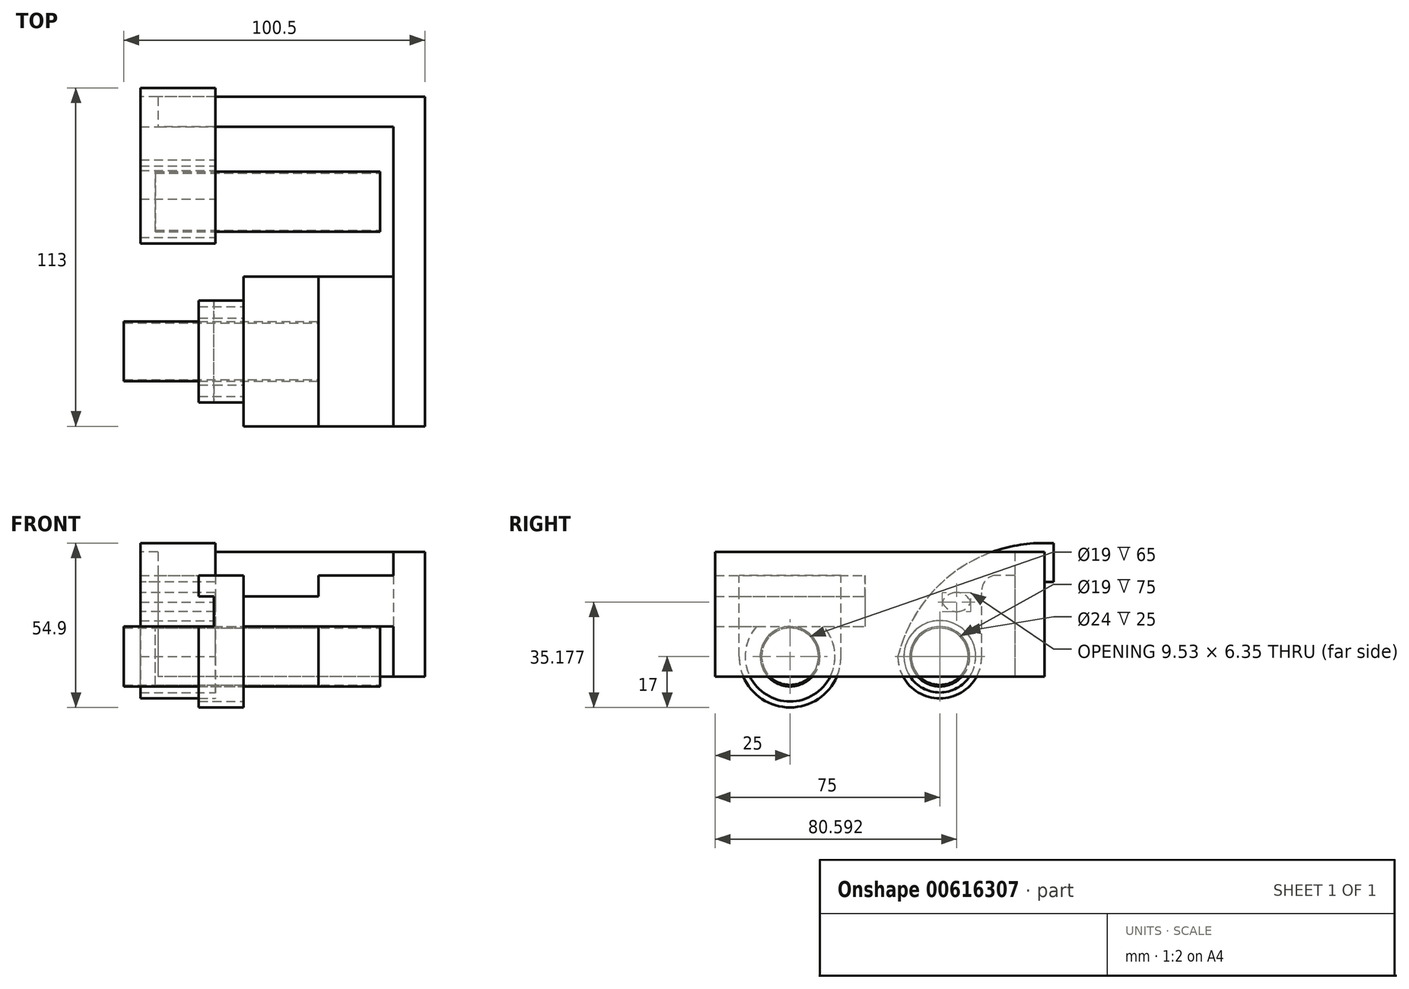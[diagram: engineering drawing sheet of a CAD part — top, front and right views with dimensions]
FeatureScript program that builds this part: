
annotation { "Feature Type Name" : "Feature", "Feature Type Description" : "" }
export const myFeature = defineFeature(function(context is Context, id is Id, definition is map)
    precondition{}
    {
        {
            var Q0;
            Q0=qCreatedBy(makeId("Front.planeOp"),FACE);
            var sketch = newSketch(context, id + "F0", { "sketchPlane" : qUnion([Q0])});
            skLineSegment(sketch, "E0.bottom", {"start": v(-30.5, 5.1) * mm, "end": v(30, 5.1) * mm});
            skLineSegment(sketch, "E0.top", {"start": v(-30.5, -5) * mm, "end": v(30, -5) * mm});
            skLineSegment(sketch, "E0.left", {"start": v(-30.5, 5.1) * mm, "end": v(-30.5, -5) * mm});
            skPoint(sketch, "E0.middle", {"position": v(0, 0) * mm});
            skLineSegment(sketch, "E1.bottom", {"start": v(-5.5, 5.1) * mm, "end": v(30, 5.1) * mm});
            skLineSegment(sketch, "E1.top", {"start": v(-5.5, 12.1) * mm, "end": v(30, 12.1) * mm});
            skLineSegment(sketch, "E1.left", {"start": v(-5.5, 5.1) * mm, "end": v(-5.5, 12.1) * mm});
            skLineSegment(sketch, "E2", {"start": v(19.5, 5.1) * mm, "end": v(19.5, 12.1) * mm});
            skLineSegment(sketch, "E3", {"start": v(30, -5) * mm, "end": v(30, 19.9) * mm});
            skLineSegment(sketch, "E4", {"start": v(30, 19.9) * mm, "end": v(19.5, 19.9) * mm});
            skLineSegment(sketch, "E5", {"start": v(19.5, 19.9) * mm, "end": v(19.5, -5) * mm});
            skLineSegment(sketch, "E6.bottom", {"start": v(19.5, -5) * mm, "end": v(30, -5) * mm});
            skLineSegment(sketch, "E6.top", {"start": v(19.5, -21.67) * mm, "end": v(30, -21.67) * mm});
            skLineSegment(sketch, "E6.left", {"start": v(19.5, -5) * mm, "end": v(19.5, -21.67) * mm});
            skLineSegment(sketch, "E6.right", {"start": v(30, -5) * mm, "end": v(30, -21.67) * mm});
            skSolve(sketch);
        }
        {
            var Q0;
            {var subQ0=sQuery(id+"F0.wireOp",EDGE,"E0.left");var subQ5=sQuery(id+"F0.wireOp",EDGE,"E2");var subQ6=sQuery(id+"F0.wireOp",EDGE,"E0.bottom");var subQ9=sQuery(id+"F0.wireOp",EDGE,"E1.left");var subQ12=sQuery(id+"F0.wireOp",EDGE,"E3");var subQ13=makeQuery(id+"F0.imprint","INTERSECT",VERTEX,{"derivedFrom":[subQ6,subQ12]});var subQ14=makeQuery(id+"F0.imprint","IMPRINT",EDGE,{"disambiguationData":[TD([[subQ13,1.0]])],"derivedFrom":subQ6});var subQ19=makeQuery(id+"F0.imprint","IMPRINT",EDGE,{"derivedFrom":subQ5});var subQ20=sQuery(id+"F0.wireOp",EDGE,"E4");Q0=qUnion([makeQuery(id+"F0.imprint","IMPRINT",FACE,{"disambiguationData":[TD([[makeQuery(id+"F0.imprint","IMPRINT",EDGE,{"derivedFrom":subQ9}),-1.0]])]}),makeQuery(id+"F0.imprint","IMPRINT",FACE,{"disambiguationData":[TD([[makeQuery(id+"F0.imprint","IMPRINT",EDGE,{"derivedFrom":sQuery(id+"F0.wireOp",EDGE,"E6.top")}),1.0]])]}),makeQuery(id+"F0.imprint","IMPRINT",FACE,{"disambiguationData":[TD([[subQ14,-1.0]])]}),makeQuery(id+"F0.imprint","IMPRINT",FACE,{"disambiguationData":[TD([[makeQuery(id+"F0.imprint","IMPRINT",EDGE,{"derivedFrom":subQ20}),1.0]])]}),makeQuery(id+"F0.imprint","IMPRINT",FACE,{"disambiguationData":[TD([[subQ19,-1.0]])]}),makeQuery(id+"F0.imprint","IMPRINT",FACE,{"disambiguationData":[TD([[makeQuery(id+"F0.imprint","IMPRINT",EDGE,{"derivedFrom":subQ0}),1.0]])]})]);}
            extrude(context, id + "F1", {"entities" : qUnion([Q0]), "depth" : 25 * mm, "offsetDistance" : 25 * mm, "hasSecondDirection" : true, "secondDirectionOppositeDirection" : true, "secondDirectionDepth" : 25 * mm});
        }
        {
            var Q0;
            Q0=makeQuery(id+"F1.opExtrude","CAP_FACE",FACE,{"disambiguationData":[OSD([sQuery(id+"F0.wireOp",EDGE,"E0.bottom"),sQuery(id+"F0.wireOp",EDGE,"E0.top"),sQuery(id+"F0.wireOp",EDGE,"E0.left"),sQuery(id+"F0.wireOp",EDGE,"E1.top"),sQuery(id+"F0.wireOp",EDGE,"E1.left"),sQuery(id+"F0.wireOp",EDGE,"E3"),sQuery(id+"F0.wireOp",EDGE,"E4"),sQuery(id+"F0.wireOp",EDGE,"E5"),sQuery(id+"F0.wireOp",EDGE,"E6.top"),sQuery(id+"F0.wireOp",EDGE,"E6.left"),sQuery(id+"F0.wireOp",EDGE,"E6.right")])],"isStart":true});
            var sketch = newSketch(context, id + "F2", { "sketchPlane" : qUnion([Q0])});
            skLineSegment(sketch, "E7.0.0", {"start": v(-19.5, 12.1) * mm, "end": v(-19.5, 19.9) * mm, "construction": true});
            skLineSegment(sketch, "E7.0.1", {"start": v(-19.5, 19.9) * mm, "end": v(-30, 19.9) * mm, "construction": true});
            skLineSegment(sketch, "E7.0.2", {"start": v(-30, 19.9) * mm, "end": v(-30, -21.67) * mm, "construction": true});
            skLineSegment(sketch, "E7.0.3", {"start": v(-30, -21.67) * mm, "end": v(-19.5, -21.67) * mm, "construction": true});
            skLineSegment(sketch, "E7.0.4", {"start": v(-19.5, -21.67) * mm, "end": v(-19.5, -5) * mm, "construction": true});
            skLineSegment(sketch, "E7.0.5", {"start": v(-19.5, -5) * mm, "end": v(30.5, -5) * mm, "construction": true});
            skLineSegment(sketch, "E7.0.6", {"start": v(30.5, -5) * mm, "end": v(30.5, 5.1) * mm, "construction": true});
            skLineSegment(sketch, "E7.0.7", {"start": v(30.5, 5.1) * mm, "end": v(5.5, 5.1) * mm, "construction": true});
            skLineSegment(sketch, "E7.0.8", {"start": v(5.5, 5.1) * mm, "end": v(5.5, 12.1) * mm, "construction": true});
            skLineSegment(sketch, "E7.0.9", {"start": v(5.5, 12.1) * mm, "end": v(-19.5, 12.1) * mm, "construction": true});
            skLineSegment(sketch, "E8.bottom", {"start": v(-30, 19.9) * mm, "end": v(-19.5, 19.9) * mm});
            skLineSegment(sketch, "E8.top", {"start": v(-30, -21.67) * mm, "end": v(-19.5, -21.67) * mm});
            skLineSegment(sketch, "E8.left", {"start": v(-30, 19.9) * mm, "end": v(-30, -21.67) * mm});
            skLineSegment(sketch, "E8.right", {"start": v(-19.5, 19.9) * mm, "end": v(-19.5, -21.67) * mm});
            skSolve(sketch);
        }
        {
            var Q0;
            Q0=qSketchRegion(id+"F2",true);
            extrude(context, id + "F3", {"entities" : qUnion([Q0]), "operationType" : NewBodyOperationType.ADD, "depth" : 50 * mm, "offsetDistance" : 25 * mm});
        }
        {
            var Q0;
            Q0=makeQuery(id+"F3.opExtrude","CAP_FACE",FACE,{"disambiguationData":[OSD([sQuery(id+"F2.wireOp",EDGE,"E8.bottom"),sQuery(id+"F2.wireOp",EDGE,"E8.top"),sQuery(id+"F2.wireOp",EDGE,"E8.left"),sQuery(id+"F2.wireOp",EDGE,"E8.right")])],"isStart":false});
            var sketch = newSketch(context, id + "F4", { "sketchPlane" : qUnion([Q0])});
            skLineSegment(sketch, "E9.0.0", {"start": v(-19.5, -21.67) * mm, "end": v(-19.5, 19.9) * mm, "construction": true});
            skLineSegment(sketch, "E9.0.1", {"start": v(-19.5, 19.9) * mm, "end": v(-30, 19.9) * mm, "construction": true});
            skLineSegment(sketch, "E9.0.2", {"start": v(-30, 19.9) * mm, "end": v(-30, -21.67) * mm, "construction": true});
            skLineSegment(sketch, "E9.0.3", {"start": v(-30, -21.67) * mm, "end": v(-19.5, -21.67) * mm, "construction": true});
            skLineSegment(sketch, "E10.bottom", {"start": v(-30, 19.9) * mm, "end": v(59.17, 19.9) * mm});
            skLineSegment(sketch, "E10.top", {"start": v(-30, -21.67) * mm, "end": v(59.17, -21.67) * mm});
            skLineSegment(sketch, "E10.left", {"start": v(-30, 19.9) * mm, "end": v(-30, -21.67) * mm});
            skLineSegment(sketch, "E10.right", {"start": v(59.17, 19.9) * mm, "end": v(59.17, -21.67) * mm});
            skSolve(sketch);
        }
        {
            var Q0;
            Q0=qSketchRegion(id+"F4",true);
            extrude(context, id + "F5", {"entities" : qUnion([Q0]), "operationType" : NewBodyOperationType.ADD, "depth" : 10 * mm, "offsetDistance" : 25 * mm});
        }
        {
            var Q0;
            Q0=makeQuery(id+"F1.opExtrude","SWEPT_FACE",FACE,{"disambiguationData":[OSD([sQuery(id+"F0.wireOp",EDGE,"E0.left")])]});
            var sketch = newSketch(context, id + "F6", { "sketchPlane" : qUnion([Q0])});
            skPoint(sketch, "E11", {"position": v(0, -15) * mm});
            skLineSegment(sketch, "E12.0", {"start": v(25, -5) * mm, "end": v(-25, -5) * mm, "construction": true});
            skCircle(sketch, "E13", {"center": v(0, -15) * mm, "radius": 10 * mm});
            skCircle(sketch, "E14", {"center": v(0, -15) * mm, "radius": 9.5 * mm});
            skSolve(sketch);
        }
        {
            var Q0;
            Q0=qSketchRegion(id+"F6",true);
            extrude(context, id + "F7", {"entities" : qUnion([Q0]), "depth" : 40 * mm, "offsetDistance" : 25 * mm, "hasSecondDirection" : true, "secondDirectionOppositeDirection" : true, "secondDirectionDepth" : 25 * mm});
        }
        {
            var Q0;
            Q0=makeQuery(id+"F1.opExtrude","SWEPT_FACE",FACE,{"disambiguationData":[OSD([sQuery(id+"F0.wireOp",EDGE,"E0.left")])]});
            var sketch = newSketch(context, id + "F8", { "sketchPlane" : qUnion([Q0])});
            skCircle(sketch, "E15.0", {"center": v(0, -15) * mm, "radius": 10 * mm, "construction": true});
            skLineSegment(sketch, "E16.0", {"start": v(25, -5) * mm, "end": v(-25, -5) * mm, "construction": true});
            skLineSegment(sketch, "E17.0", {"start": v(25, 5.1) * mm, "end": v(-25, 5.1) * mm, "construction": true});
            skCircle(sketch, "E18", {"center": v(0, -15) * mm, "radius": 15 * mm});
            skCircle(sketch, "E19", {"center": v(0, -15) * mm, "radius": 17 * mm});
            skLineSegment(sketch, "E20", {"start": v(0, -15) * mm, "end": v(20.33, -15) * mm, "construction": true});
            skLineSegment(sketch, "E21", {"start": v(17, -15) * mm, "end": v(17, -5) * mm});
            skLineSegment(sketch, "E22", {"start": v(-17, -15) * mm, "end": v(-17, -5) * mm});
            skLineSegment(sketch, "E23", {"start": v(-17, -5) * mm, "end": v(17, -5) * mm});
            skLineSegment(sketch, "E24", {"start": v(-17, -5) * mm, "end": v(-17, 5.1) * mm});
            skLineSegment(sketch, "E25", {"start": v(-17, 5.1) * mm, "end": v(17, 5.1) * mm});
            skLineSegment(sketch, "E26", {"start": v(17, 5.1) * mm, "end": v(17, -5) * mm});
            skLineSegment(sketch, "E27.0", {"start": v(25, 12.1) * mm, "end": v(-25, 12.1) * mm, "construction": true});
            skLineSegment(sketch, "E28", {"start": v(-17, 5.1) * mm, "end": v(-17, 12.1) * mm});
            skLineSegment(sketch, "E29", {"start": v(-17, 12.1) * mm, "end": v(17, 12.1) * mm});
            skLineSegment(sketch, "E30", {"start": v(17, 12.1) * mm, "end": v(17, 5.1) * mm});
            skSolve(sketch);
        }
        {
            var Q0;
            {var subQ3=sQuery(id+"F8.wireOp",EDGE,"E23");var subQ6=sQuery(id+"F8.wireOp",EDGE,"E18");var subQ7=makeQuery(id+"F8.imprint","INTERSECT",VERTEX,{"disambiguationData":[OD(0.0)],"derivedFrom":[subQ6,subQ3]});Q0=makeQuery(id+"F8.imprint","IMPRINT",FACE,{"disambiguationData":[TD([[makeQuery(id+"F8.imprint","IMPRINT",EDGE,{"disambiguationData":[TD([[subQ7,1.0]])],"derivedFrom":subQ6}),-1.0]])]});}
            var Q1;
            {var subQ0=sQuery(id+"F8.wireOp",EDGE,"E22");Q1=makeQuery(id+"F8.imprint","IMPRINT",FACE,{"disambiguationData":[TD([[makeQuery(id+"F8.imprint","IMPRINT",EDGE,{"derivedFrom":subQ0}),-1.0]])]});}
            var Q2;
            {var subQ0=sQuery(id+"F8.wireOp",EDGE,"E21");Q2=makeQuery(id+"F8.imprint","IMPRINT",FACE,{"disambiguationData":[TD([[makeQuery(id+"F8.imprint","IMPRINT",EDGE,{"derivedFrom":subQ0}),1.0]])]});}
            var Q3;
            {var subQ0=sQuery(id+"F8.wireOp",EDGE,"E24");Q3=makeQuery(id+"F8.imprint","IMPRINT",FACE,{"disambiguationData":[TD([[makeQuery(id+"F8.imprint","IMPRINT",EDGE,{"derivedFrom":subQ0}),-1.0]])]});}
            var Q4;
            {var subQ0=sQuery(id+"F8.wireOp",EDGE,"E23");var subQ1=sQuery(id+"F8.wireOp",EDGE,"E18");var subQ2=makeQuery(id+"F8.imprint","INTERSECT",VERTEX,{"disambiguationData":[OD(0.0)],"derivedFrom":[subQ1,subQ0]});Q4=makeQuery(id+"F8.imprint","IMPRINT",FACE,{"disambiguationData":[TD([[makeQuery(id+"F8.imprint","IMPRINT",EDGE,{"disambiguationData":[TD([[subQ2,-1.0]])],"derivedFrom":subQ1}),-1.0]])]});}
            var Q5;
            {var subQ0=sQuery(id+"F8.wireOp",EDGE,"E23");var subQ1=sQuery(id+"F8.wireOp",EDGE,"E18");var subQ2=makeQuery(id+"F8.imprint","INTERSECT",VERTEX,{"disambiguationData":[OD(0.0)],"derivedFrom":[subQ1,subQ0]});Q5=makeQuery(id+"F8.imprint","IMPRINT",FACE,{"disambiguationData":[TD([[makeQuery(id+"F8.imprint","IMPRINT",EDGE,{"disambiguationData":[TD([[subQ2,-1.0]])],"derivedFrom":subQ1}),1.0]])]});}
            var Q6;
            Q6=makeQuery(id+"F8.imprint","IMPRINT",FACE,{"disambiguationData":[TD([[makeQuery(id+"F8.imprint","IMPRINT",EDGE,{"derivedFrom":sQuery(id+"F8.wireOp",EDGE,"E25")}),-1.0]])]});
            extrude(context, id + "F9", {"entities" : qUnion([Q0, Q1, Q2, Q3, Q4, Q5, Q6]), "depth" : 10 * mm, "offsetDistance" : 25 * mm});
        }
        {
            var Q0;
            Q0=makeQuery(id+"F9.opExtrude","CAP_FACE",FACE,{"disambiguationData":[OSD([sQuery(id+"F8.wireOp",EDGE,"E18"),sQuery(id+"F8.wireOp",EDGE,"E19"),sQuery(id+"F8.wireOp",EDGE,"E21"),sQuery(id+"F8.wireOp",EDGE,"E22"),sQuery(id+"F8.wireOp",EDGE,"E23"),sQuery(id+"F8.wireOp",EDGE,"E24"),sQuery(id+"F8.wireOp",EDGE,"E26"),sQuery(id+"F8.wireOp",EDGE,"E28"),sQuery(id+"F8.wireOp",EDGE,"E29"),sQuery(id+"F8.wireOp",EDGE,"E30")])],"isStart":true});
            var sketch = newSketch(context, id + "F10", { "sketchPlane" : qUnion([Q0])});
            skLineSegment(sketch, "E31.0", {"start": v(-25, 12.1) * mm, "end": v(25, 12.1) * mm, "construction": true});
            skLineSegment(sketch, "E32.0", {"start": v(-25, 5.1) * mm, "end": v(25, 5.1) * mm, "construction": true});
            skLineSegment(sketch, "E33.0", {"start": v(17, -15) * mm, "end": v(17, 12.1) * mm, "construction": true});
            skLineSegment(sketch, "E34.0", {"start": v(-17, -15) * mm, "end": v(-17, 12.1) * mm, "construction": true});
            skLineSegment(sketch, "E35.bottom", {"start": v(17, 12.1) * mm, "end": v(-17, 12.1) * mm});
            skLineSegment(sketch, "E35.top", {"start": v(17, 5.1) * mm, "end": v(-17, 5.1) * mm});
            skLineSegment(sketch, "E35.left", {"start": v(17, 12.1) * mm, "end": v(17, 5.1) * mm});
            skLineSegment(sketch, "E35.right", {"start": v(-17, 12.1) * mm, "end": v(-17, 5.1) * mm});
            skArc(sketch, "E36.0", {"start": v(11.18, -5) * mm, "mid": v(0, -30) * mm, "end": v(-11.18, -5) * mm});
            skLineSegment(sketch, "E37.0", {"start": v(-25, -5) * mm, "end": v(25, -5) * mm, "construction": true});
            skPoint(sketch, "E38.0", {"position": v(17, -15) * mm});
            skPoint(sketch, "E39.0", {"position": v(-17, -15) * mm});
            skArc(sketch, "E40.0", {"start": v(17, -15) * mm, "mid": v(0, -32) * mm, "end": v(-17, -15) * mm});
            skArc(sketch, "E41.0.0", {"start": v(-17, -15) * mm, "mid": v(0, -32) * mm, "end": v(17, -15) * mm, "construction": true});
            skLineSegment(sketch, "E41.0.2", {"start": v(17, 12.1) * mm, "end": v(-17, 12.1) * mm, "construction": true});
            skLineSegment(sketch, "E41.0.3", {"start": v(-17, 12.1) * mm, "end": v(-17, -15) * mm, "construction": true});
            skLineSegment(sketch, "E42", {"start": v(-17, -15) * mm, "end": v(-17, -5) * mm});
            skLineSegment(sketch, "E43", {"start": v(-17, -5) * mm, "end": v(17, -5) * mm});
            skLineSegment(sketch, "E44", {"start": v(17, -5) * mm, "end": v(17, -15) * mm});
            skSolve(sketch);
        }
        {
            var Q0;
            Q0=makeQuery(id+"F10.imprint","IMPRINT",FACE,{"disambiguationData":[TD([[makeQuery(id+"F10.imprint","IMPRINT",EDGE,{"derivedFrom":sQuery(id+"F10.wireOp",EDGE,"E35.bottom")}),1.0]])]});
            var Q1;
            {var subQ1=sQuery(id+"F10.wireOp",EDGE,"E36.0");Q1=makeQuery(id+"F10.imprint","IMPRINT",FACE,{"disambiguationData":[TD([[makeQuery(id+"F10.imprint","IMPRINT",EDGE,{"derivedFrom":subQ1}),1.0]])]});}
            extrude(context, id + "F11", {"entities" : qUnion([Q0, Q1]), "operationType" : NewBodyOperationType.ADD, "oppositeDirection" : true, "depth" : 15 * mm, "offsetDistance" : 25 * mm});
        }
        {
            var Q0;
            Q0=qCreatedBy(makeId("Right.planeOp"),FACE);
            var sketch = newSketch(context, id + "F12", { "sketchPlane" : qUnion([Q0])});
            skLineSegment(sketch, "E45", {"start": v(0, 0) * mm, "end": v(71.15, 0) * mm, "construction": true});
            skCircle(sketch, "E46.0", {"center": v(0, -15) * mm, "radius": 9.5 * mm, "construction": true});
            skCircle(sketch, "E47.0", {"center": v(0, -15) * mm, "radius": 10 * mm, "construction": true});
            skLineSegment(sketch, "E48", {"start": v(0, -15) * mm, "end": v(68.73, -15) * mm, "construction": true});
            skLineSegment(sketch, "E49.0", {"start": v(75, 19.9) * mm, "end": v(75, -21.67) * mm, "construction": true});
            skLineSegment(sketch, "E50.0", {"start": v(25, 5.1) * mm, "end": v(25, -5) * mm, "construction": true});
            skCircle(sketch, "E51", {"center": v(50, -15) * mm, "radius": 9.5 * mm});
            skCircle(sketch, "E52", {"center": v(50, -15) * mm, "radius": 10 * mm});
            skSolve(sketch);
        }
        {
            var Q0;
            Q0=qSketchRegion(id+"F12",true);
            extrude(context, id + "F13", {"entities" : qUnion([Q0]), "oppositeDirection" : true, "depth" : 60 * mm, "offsetDistance" : 25 * mm, "hasSecondDirection" : true, "secondDirectionOppositeDirection" : false, "secondDirectionDepth" : 15 * mm});
        }
        {
            var Q0;
            Q0=qCreatedBy(makeId("Right.planeOp"),FACE);
            cPlane(context, id + "F14", {"entities" : qUnion([Q0]), "cplaneType" : CPlaneType.OFFSET, "offset" : 40 * mm, "oppositeDirection" : true, "width" : 150 * mm, "height" : 150 * mm});
        }
        {
            var Q0;
            Q0=qCreatedBy(id+"F14.planeOp",FACE);
            var sketch = newSketch(context, id + "F15", { "sketchPlane" : qUnion([Q0])});
            skCircle(sketch, "E53.0", {"center": v(50, -15) * mm, "radius": 9.5 * mm});
            skCircle(sketch, "E54.0", {"center": v(50, -15) * mm, "radius": 10 * mm});
            skCircle(sketch, "E55", {"center": v(50, -15) * mm, "radius": 12 * mm});
            skCircle(sketch, "E56", {"center": v(50, -15) * mm, "radius": 14 * mm});
            skLineSegment(sketch, "E57.0", {"start": v(-25, 12.1) * mm, "end": v(10, 12.1) * mm, "construction": true});
            skLineSegment(sketch, "E58.0", {"start": v(75, 12.1) * mm, "end": v(75, -21.67) * mm, "construction": true});
            skLineSegment(sketch, "E59", {"start": v(36, -15) * mm, "end": v(36, 12.1) * mm});
            skLineSegment(sketch, "E60", {"start": v(64, -15) * mm, "end": v(64, 12.1) * mm});
            skLineSegment(sketch, "E61", {"start": v(64, 12.1) * mm, "end": v(36, 12.1) * mm});
            skLineSegment(sketch, "E62.top", {"start": v(75, 12.1) * mm, "end": v(36, 12.1) * mm});
            skLineSegment(sketch, "E63.0.1", {"start": v(10, 5.1) * mm, "end": v(-25, 5.1) * mm, "construction": true});
            skLineSegment(sketch, "E63.0.2", {"start": v(-25, 5.1) * mm, "end": v(-25, 12.1) * mm, "construction": true});
            skPoint(sketch, "E62.left.start.orphan", {"position": v(75, 19.9) * mm});
            skLineSegment(sketch, "E64.right", {"start": v(36, 12.1) * mm, "end": v(36, 5.1) * mm});
            skLineSegment(sketch, "E65.left", {"start": v(75, 19.9) * mm, "end": v(75, 12.1) * mm});
            skLineSegment(sketch, "E66", {"start": v(75, 19.9) * mm, "end": v(36, 12.1) * mm});
            skLineSegment(sketch, "E67.bottom", {"start": v(75, 19.9) * mm, "end": v(36, 19.9) * mm});
            skLineSegment(sketch, "E67.right", {"start": v(36, 19.9) * mm, "end": v(36, 12.1) * mm});
            skPoint(sketch, "E63.0.0.end.orphan", {"position": v(25, 5.1) * mm});
            skPoint(sketch, "E63.0.0.start.orphan", {"position": v(25, 12.1) * mm});
            skSolve(sketch);
        }
        {
            var Q0;
            Q0=qSketchRegion(id+"F15",true);
            var Q1;
            Q1=makeQuery(id+"F3.boolean.opBoolean","MERGE",FACE,{"derivedFrom":[makeQuery(id+"F1.opExtrude","SWEPT_FACE",FACE,{"disambiguationData":[OSD([sQuery(id+"F0.wireOp",EDGE,"E5")])]}),makeQuery(id+"F1.opExtrude","SWEPT_FACE",FACE,{"disambiguationData":[OSD([sQuery(id+"F0.wireOp",EDGE,"E6.left")])]}),makeQuery(id+"F3.opExtrude","SWEPT_FACE",FACE,{"disambiguationData":[OSD([sQuery(id+"F2.wireOp",EDGE,"E8.right")])]})]});
            extrude(context, id + "F16", {"entities" : qUnion([Q0]), "oppositeDirection" : true, "depth" : 25 * mm, "endBoundEntityFace" : qUnion([Q1]), "offsetDistance" : 25 * mm});
        }
        {
            var Q0;
            Q0=makeQuery(id+"F16.opExtrude","SWEPT_FACE",FACE,{"disambiguationData":[OSD([sQuery(id+"F15.wireOp",EDGE,"E67.bottom")])]});
            var sketch = newSketch(context, id + "F17", { "sketchPlane" : qUnion([Q0])});
            skLineSegment(sketch, "E68.0.0", {"start": v(30, -25) * mm, "end": v(30, 85) * mm, "construction": true});
            skLineSegment(sketch, "E68.0.1", {"start": v(30, 85) * mm, "end": v(-59.17, 85) * mm, "construction": true});
            skLineSegment(sketch, "E68.0.2", {"start": v(-59.17, 85) * mm, "end": v(-59.17, 75) * mm, "construction": true});
            skLineSegment(sketch, "E68.0.3", {"start": v(-59.17, 75) * mm, "end": v(19.5, 75) * mm, "construction": true});
            skLineSegment(sketch, "E68.0.4", {"start": v(19.5, 75) * mm, "end": v(19.5, -25) * mm, "construction": true});
            skLineSegment(sketch, "E68.0.5", {"start": v(19.5, -25) * mm, "end": v(30, -25) * mm, "construction": true});
            skLineSegment(sketch, "E69", {"start": v(15, 40) * mm, "end": v(-60, 40) * mm, "construction": true});
            skLineSegment(sketch, "E70", {"start": v(-60, 60) * mm, "end": v(15, 60) * mm, "construction": true});
            skLineSegment(sketch, "E71.bottom", {"start": v(-40, 36) * mm, "end": v(-65, 36) * mm});
            skLineSegment(sketch, "E71.top", {"start": v(-40, 85) * mm, "end": v(-65, 85) * mm});
            skLineSegment(sketch, "E71.left", {"start": v(-40, 36) * mm, "end": v(-40, 85) * mm});
            skLineSegment(sketch, "E71.right", {"start": v(-65, 36) * mm, "end": v(-65, 85) * mm});
            skSolve(sketch);
        }
        {
            var Q0;
            Q0=qSketchRegion(id+"F17",true);
            extrude(context, id + "F18", {"entities" : qUnion([Q0]), "operationType" : NewBodyOperationType.ADD, "depth" : 3 * mm, "offsetDistance" : 25 * mm});
        }
        {
            var Q0;
            Q0=makeQuery(id+"F18.opExtrude","SWEPT_FACE",FACE,{"disambiguationData":[OSD([sQuery(id+"F17.wireOp",EDGE,"E71.top")])]});
            var sketch = newSketch(context, id + "F19", { "sketchPlane" : qUnion([Q0])});
            skLineSegment(sketch, "E72.0.0", {"start": v(40, 19.9) * mm, "end": v(65, 19.9) * mm, "construction": true});
            skLineSegment(sketch, "E72.0.1", {"start": v(65, 19.9) * mm, "end": v(65, 22.9) * mm, "construction": true});
            skLineSegment(sketch, "E72.0.2", {"start": v(65, 22.9) * mm, "end": v(40, 22.9) * mm, "construction": true});
            skLineSegment(sketch, "E72.0.3", {"start": v(40, 22.9) * mm, "end": v(40, 19.9) * mm, "construction": true});
            skLineSegment(sketch, "E73.bottom", {"start": v(40, 22.9) * mm, "end": v(65, 22.9) * mm});
            skLineSegment(sketch, "E73.top", {"start": v(40, 9.9) * mm, "end": v(65, 9.9) * mm});
            skLineSegment(sketch, "E73.left", {"start": v(40, 22.9) * mm, "end": v(40, 9.9) * mm});
            skLineSegment(sketch, "E73.right", {"start": v(65, 22.9) * mm, "end": v(65, 9.9) * mm});
            skSolve(sketch);
        }
        {
            var Q0;
            Q0=qSketchRegion(id+"F19",true);
            extrude(context, id + "F20", {"entities" : qUnion([Q0]), "operationType" : NewBodyOperationType.ADD, "depth" : 3 * mm, "offsetDistance" : 25 * mm});
        }
        {
            var Q0;
            Q0=makeQuery(id+"F18.opExtrude","CAP_EDGE",EDGE,{"disambiguationData":[OSD([sQuery(id+"F17.wireOp",EDGE,"E71.bottom")])],"isStart":false});
            fillet(context, id + "F21", {"entities" : qUnion([Q0]), "radius" : 50 * mm, "tangentPropagation" : true, "allowEdgeOverflow" : false});
        }
        {
            var Q0;
            Q0=makeQuery(id+"F20.boolean.opBoolean","MERGE",FACE,{"derivedFrom":[makeQuery(id+"F18.boolean.opBoolean","MERGE",FACE,{"derivedFrom":[makeQuery(id+"F16.opExtrude","CAP_FACE",FACE,{"disambiguationData":[OSD([sQuery(id+"F15.wireOp",EDGE,"E55"),sQuery(id+"F15.wireOp",EDGE,"E56"),sQuery(id+"F15.wireOp",EDGE,"E59"),sQuery(id+"F15.wireOp",EDGE,"E60"),sQuery(id+"F15.wireOp",EDGE,"E64.bottom"),sQuery(id+"F15.wireOp",EDGE,"E64.top"),sQuery(id+"F15.wireOp",EDGE,"E64.left"),sQuery(id+"F15.wireOp",EDGE,"E67.bottom"),sQuery(id+"F15.wireOp",EDGE,"E62.top"),sQuery(id+"F15.wireOp",EDGE,"E65.left"),sQuery(id+"F15.wireOp",EDGE,"E67.right")])],"isStart":false}),makeQuery(id+"F18.opExtrude","SWEPT_FACE",FACE,{"disambiguationData":[OSD([sQuery(id+"F17.wireOp",EDGE,"E71.right")])]})]}),makeQuery(id+"F20.opExtrude","SWEPT_FACE",FACE,{"disambiguationData":[OSD([sQuery(id+"F19.wireOp",EDGE,"E73.right")])]})]});
            var sketch = newSketch(context, id + "F22", { "sketchPlane" : qUnion([Q0])});
            skLineSegment(sketch, "E74.0", {"start": v(-13.3, 8.4) * mm, "end": v(-13.3, 8.8) * mm});
            skLineSegment(sketch, "E74.3", {"start": v(-50.48, 0) * mm, "end": v(-50.48, 8.4) * mm});
            skLineSegment(sketch, "E74.5", {"start": v(-60.7, 6.35) * mm, "end": v(-60.7, 0) * mm});
            skLineSegment(sketch, "E75", {"start": v(-50.48, 6.35) * mm, "end": v(-50.48, 8.4) * mm});
            skLineSegment(sketch, "E76", {"start": v(-50.48, 6.35) * mm, "end": v(-60.7, 6.35) * mm});
            skLineSegment(sketch, "E77", {"start": v(-60.7, 0) * mm, "end": v(-50.48, 0) * mm});
            skSolve(sketch);
        }
        {
            var Q0;
            Q0=makeQuery(id+"F22.imprint","IMPRINT",FACE,{"disambiguationData":[TD([[makeQuery(id+"F22.imprint","IMPRINT",EDGE,{"derivedFrom":sQuery(id+"F22.wireOp",EDGE,"E74.5")}),1.0]])]});
            extrude(context, id + "F23", {"entities" : qUnion([Q0]), "operationType" : NewBodyOperationType.REMOVE, "oppositeDirection" : true, "depth" : 25 * mm, "offsetDistance" : 25 * mm});
        }
        {
            var Q0;
            {var subQ0=sQuery(id+"F22.wireOp",EDGE,"E76");Q0=qUnion([makeQuery(id+"F23.boolean.opBoolean","COPY",EDGE,{"derivedFrom":makeQuery(id+"F23.opExtrude","SWEPT_EDGE",EDGE,{"disambiguationData":[OSD([sQuery(id+"F22.wireOp",EDGE,"E74.3"),subQ0])]})}),makeQuery(id+"F23.boolean.opBoolean","COPY",EDGE,{"derivedFrom":makeQuery(id+"F23.opExtrude","SWEPT_EDGE",EDGE,{"disambiguationData":[OSD([sQuery(id+"F22.wireOp",EDGE,"E74.5"),subQ0])]})})]);}
            var Q1;
            Q1=makeQuery(id+"F16.opExtrude","SWEPT_EDGE",EDGE,{"disambiguationData":[OSD([sQuery(id+"F15.wireOp",EDGE,"E59"),sQuery(id+"F15.wireOp",EDGE,"E64.top"),sQuery(id+"F15.wireOp",EDGE,"E64.right")])]});
            var Q2;
            Q2=makeQuery(id+"F16.opExtrude","SWEPT_EDGE",EDGE,{"disambiguationData":[OSD([sQuery(id+"F15.wireOp",EDGE,"E60"),sQuery(id+"F15.wireOp",EDGE,"E62.top")])]});
            var Q3;
            Q3=makeQuery(id+"F23.boolean.opBoolean","COPY",EDGE,{"derivedFrom":makeQuery(id+"F23.opExtrude","SWEPT_EDGE",EDGE,{"disambiguationData":[OSD([sQuery(id+"F22.wireOp",EDGE,"E74.5"),sQuery(id+"F22.wireOp",EDGE,"E76")])]})});
            var Q4;
            Q4=makeQuery(id+"F23.boolean.opBoolean","COPY",EDGE,{"derivedFrom":makeQuery(id+"F23.opExtrude","SWEPT_EDGE",EDGE,{"disambiguationData":[OSD([sQuery(id+"F22.wireOp",EDGE,"E74.3"),sQuery(id+"F22.wireOp",EDGE,"E77")])]})});
            var Q5;
            Q5=makeQuery(id+"F23.boolean.opBoolean","COPY",EDGE,{"derivedFrom":makeQuery(id+"F23.opExtrude","SWEPT_EDGE",EDGE,{"disambiguationData":[OSD([sQuery(id+"F22.wireOp",EDGE,"E74.5"),sQuery(id+"F22.wireOp",EDGE,"E77")])]})});
            fillet(context, id + "F24", {"entities" : qUnion([Q0, Q1, Q2, Q3, Q4, Q5]), "radius" : 5 * mm, "tangentPropagation" : true, "allowEdgeOverflow" : false});
        }
    });
